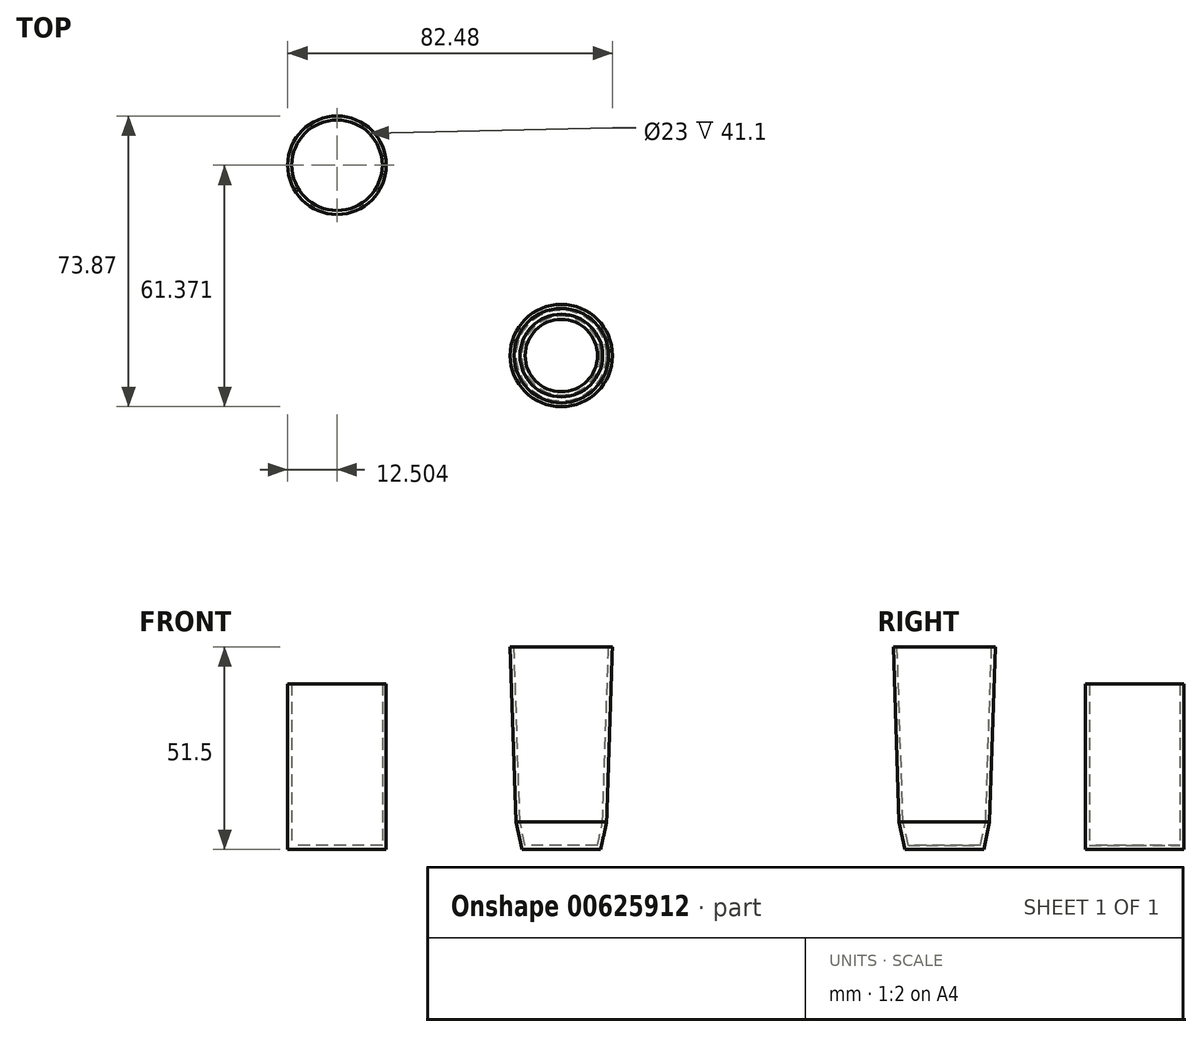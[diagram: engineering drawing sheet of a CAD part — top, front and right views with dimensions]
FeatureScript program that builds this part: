
annotation { "Feature Type Name" : "Feature", "Feature Type Description" : "" }
export const myFeature = defineFeature(function(context is Context, id is Id, definition is map)
    precondition{}
    {
        {
            var Q0;
            Q0=qCreatedBy(makeId("Top.planeOp"),FACE);
            var sketch = newSketch(context, id + "F0", { "sketchPlane" : qUnion([Q0])});
            skCircle(sketch, "E0", {"center": v(0, 0) * mm, "radius": 10 * mm});
            skSolve(sketch);
        }
        {
            var Q0;
            Q0=qCreatedBy(makeId("Top.planeOp"),FACE);
            cPlane(context, id + "F1", {"entities" : qUnion([Q0]), "cplaneType" : CPlaneType.OFFSET, "offset" : 7 * mm, "width" : 150 * mm, "height" : 150 * mm});
        }
        {
            var Q0;
            Q0=qCreatedBy(id+"F1.planeOp",FACE);
            var sketch = newSketch(context, id + "F2", { "sketchPlane" : qUnion([Q0])});
            skCircle(sketch, "E1", {"center": v(0, 0) * mm, "radius": 11.5 * mm});
            skSolve(sketch);
        }
        {
            var Q0;
            Q0=makeQuery(id+"F0.imprint","IMPRINT",FACE,{"disambiguationData":[TD([[makeQuery(id+"F0.imprint","IMPRINT",EDGE,{"derivedFrom":sQuery(id+"F0.wireOp",EDGE,"E0")}),1.0]])]});
            var Q1;
            Q1=makeQuery(id+"F2.imprint","IMPRINT",FACE,{"disambiguationData":[TD([[makeQuery(id+"F2.imprint","IMPRINT",EDGE,{"derivedFrom":sQuery(id+"F2.wireOp",EDGE,"E1")}),1.0]])]});
            loft(context, id + "F3", {"sheetProfilesArray" : [{ "sheetProfileEntities" : qUnion([Q0]) }, { "sheetProfileEntities" : qUnion([Q1]) }]});
        }
        {
            var Q0;
            Q0=makeQuery(id+"F3.opLoft","CAP_FACE",FACE,{"disambiguationData":[OSD([makeQuery(id+"F2.imprint","IMPRINT",FACE,{"disambiguationData":[TD([[makeQuery(id+"F2.imprint","IMPRINT",EDGE,{"derivedFrom":sQuery(id+"F2.wireOp",EDGE,"E1")}),1.0]])]})])],"isStart":true});
            var sketch = newSketch(context, id + "F4", { "sketchPlane" : qUnion([Q0])});
            skCircle(sketch, "E2", {"center": v(0, 0) * mm, "radius": 11.5 * mm});
            skSolve(sketch);
        }
        {
            var Q0;
            Q0=qCreatedBy(id+"F1.planeOp",FACE);
            cPlane(context, id + "F5", {"entities" : qUnion([Q0]), "cplaneType" : CPlaneType.OFFSET, "offset" : 44.5 * mm, "width" : 150 * mm, "height" : 150 * mm});
        }
        {
            var Q0;
            Q0=qCreatedBy(id+"F5.planeOp",FACE);
            var sketch = newSketch(context, id + "F6", { "sketchPlane" : qUnion([Q0])});
            skCircle(sketch, "E3", {"center": v(0, 0) * mm, "radius": 13 * mm});
            skSolve(sketch);
        }
        {
            var Q1;
            Q1=makeQuery(id+"F4.imprint","IMPRINT",FACE,{"disambiguationData":[TD([[makeQuery(id+"F4.imprint","IMPRINT",EDGE,{"derivedFrom":sQuery(id+"F4.wireOp",EDGE,"E2")}),1.0]])]});
            var Q2;
            Q2=makeQuery(id+"F6.imprint","IMPRINT",FACE,{"disambiguationData":[TD([[makeQuery(id+"F6.imprint","IMPRINT",EDGE,{"derivedFrom":sQuery(id+"F6.wireOp",EDGE,"E3")}),1.0]])]});
            loft(context, id + "F7", {"operationType" : NewBodyOperationType.ADD, "sheetProfilesArray" : [{ "sheetProfileEntities" : qUnion([Q1]) }, { "sheetProfileEntities" : qUnion([Q2]) }]});
        }
        {
            var Q0;
            Q0=makeQuery(id+"F7.opLoft","CAP_FACE",FACE,{"disambiguationData":[OSD([makeQuery(id+"F6.imprint","IMPRINT",FACE,{"disambiguationData":[TD([[makeQuery(id+"F6.imprint","IMPRINT",EDGE,{"derivedFrom":sQuery(id+"F6.wireOp",EDGE,"E3")}),1.0]])]})])],"isStart":true});
            shell(context, id + "F8", {"entities" : qUnion([Q0]), "thickness" : 1 * mm});
        }
        {
            var Q0;
            Q0=qCreatedBy(makeId("Top.planeOp"),FACE);
            var sketch = newSketch(context, id + "F9", { "sketchPlane" : qUnion([Q0])});
            skCircle(sketch, "E4", {"center": v(-56.98, 48.37) * mm, "radius": 12.5 * mm});
            skSolve(sketch);
        }
        {
            var Q0;
            Q0=makeQuery(id+"F9.imprint","IMPRINT",FACE,{"disambiguationData":[TD([[makeQuery(id+"F9.imprint","IMPRINT",EDGE,{"derivedFrom":sQuery(id+"F9.wireOp",EDGE,"E4")}),1.0]])]});
            extrude(context, id + "F10", {"entities" : qUnion([Q0]), "depth" : 42.1 * mm, "offsetDistance" : 25 * mm});
        }
        {
            var Q0;
            Q0=makeQuery(id+"F10.opExtrude","CAP_FACE",FACE,{"disambiguationData":[OSD([sQuery(id+"F9.wireOp",EDGE,"E4")])],"isStart":false});
            shell(context, id + "F11", {"entities" : qUnion([Q0]), "thickness" : 1 * mm});
        }
    });
